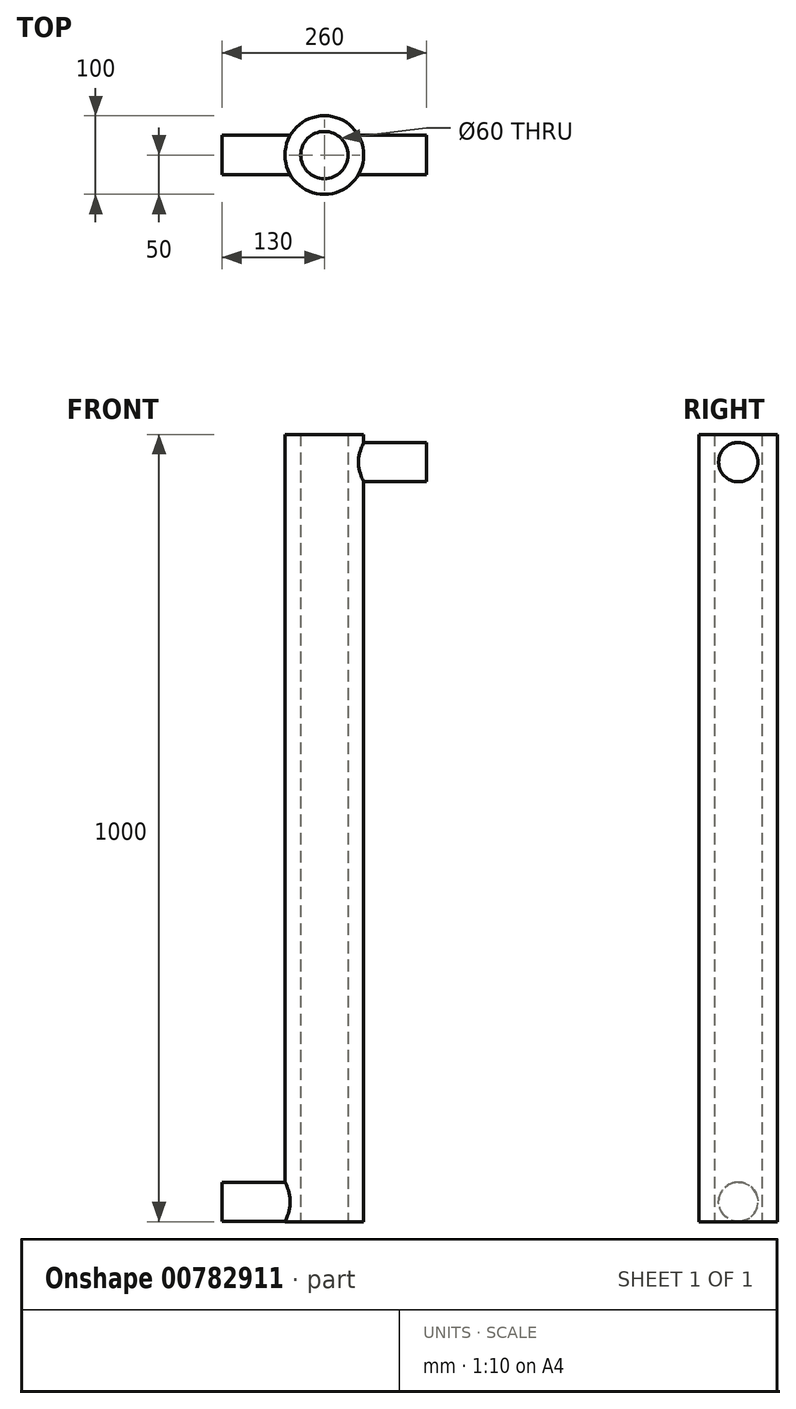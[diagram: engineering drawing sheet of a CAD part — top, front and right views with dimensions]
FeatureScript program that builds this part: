
annotation { "Feature Type Name" : "Feature", "Feature Type Description" : "" }
export const myFeature = defineFeature(function(context is Context, id is Id, definition is map)
    precondition{}
    {
        {
            var Q0;
            Q0=qCreatedBy(makeId("Top.planeOp"),FACE);
            var sketch = newSketch(context, id + "F0", { "sketchPlane" : qUnion([Q0])});
            skCircle(sketch, "E0", {"center": v(0, 0) * mm, "radius": 30 * mm});
            skCircle(sketch, "E1", {"center": v(0, 0) * mm, "radius": 50 * mm});
            skSolve(sketch);
        }
        {
            var Q0;
            Q0 = qSketchRegion(id + "F0", true);
            extrude(context, id + "F1", {"entities" : qUnion([Q0]), "depth" : 1000 * mm, "offsetDistance" : 25 * mm});
        }
        {
            var Q0;
            Q0=qCreatedBy(makeId("Right.planeOp"),FACE);
            cPlane(context, id + "F2", {"entities" : qUnion([Q0]), "cplaneType" : CPlaneType.OFFSET, "offset" : 130 * mm, "oppositeDirection" : true, "width" : 150 * mm, "height" : 150 * mm});
        }
        {
            var Q0;
            Q0=qCreatedBy(id+"F2.planeOp",FACE);
            var sketch = newSketch(context, id + "F3", { "sketchPlane" : qUnion([Q0])});
            skCircle(sketch, "E2", {"center": v(0, 25.23) * mm, "radius": 25 * mm});
            skSolve(sketch);
        }
        {
            var Q0;
            Q0 = qSketchRegion(id + "F3", true);
            extrude(context, id + "F4", {"entities" : qUnion([Q0]), "operationType" : NewBodyOperationType.ADD, "depth" : 100 * mm, "offsetDistance" : 25 * mm});
        }
        {
            var Q0;
            Q0=qCreatedBy(makeId("Right.planeOp"),FACE);
            cPlane(context, id + "F5", {"entities" : qUnion([Q0]), "cplaneType" : CPlaneType.OFFSET, "offset" : 130 * mm, "width" : 150 * mm, "height" : 150 * mm});
        }
        {
            var Q0;
            Q0=qCreatedBy(id+"F5.planeOp",FACE);
            var sketch = newSketch(context, id + "F6", { "sketchPlane" : qUnion([Q0])});
            skCircle(sketch, "E3", {"center": v(0, 964.9) * mm, "radius": 25 * mm});
            skSolve(sketch);
        }
        {
            var Q0;
            Q0=makeQuery(id+"F6.imprint","IMPRINT",FACE,{"disambiguationData":[TD([[makeQuery(id+"F6.imprint","IMPRINT",EDGE,{"derivedFrom":sQuery(id+"F6.wireOp",EDGE,"E3")}),1.0]])]});
            extrude(context, id + "F7", {"entities" : qUnion([Q0]), "operationType" : NewBodyOperationType.ADD, "oppositeDirection" : true, "depth" : 100 * mm, "offsetDistance" : 25 * mm});
        }
    });
